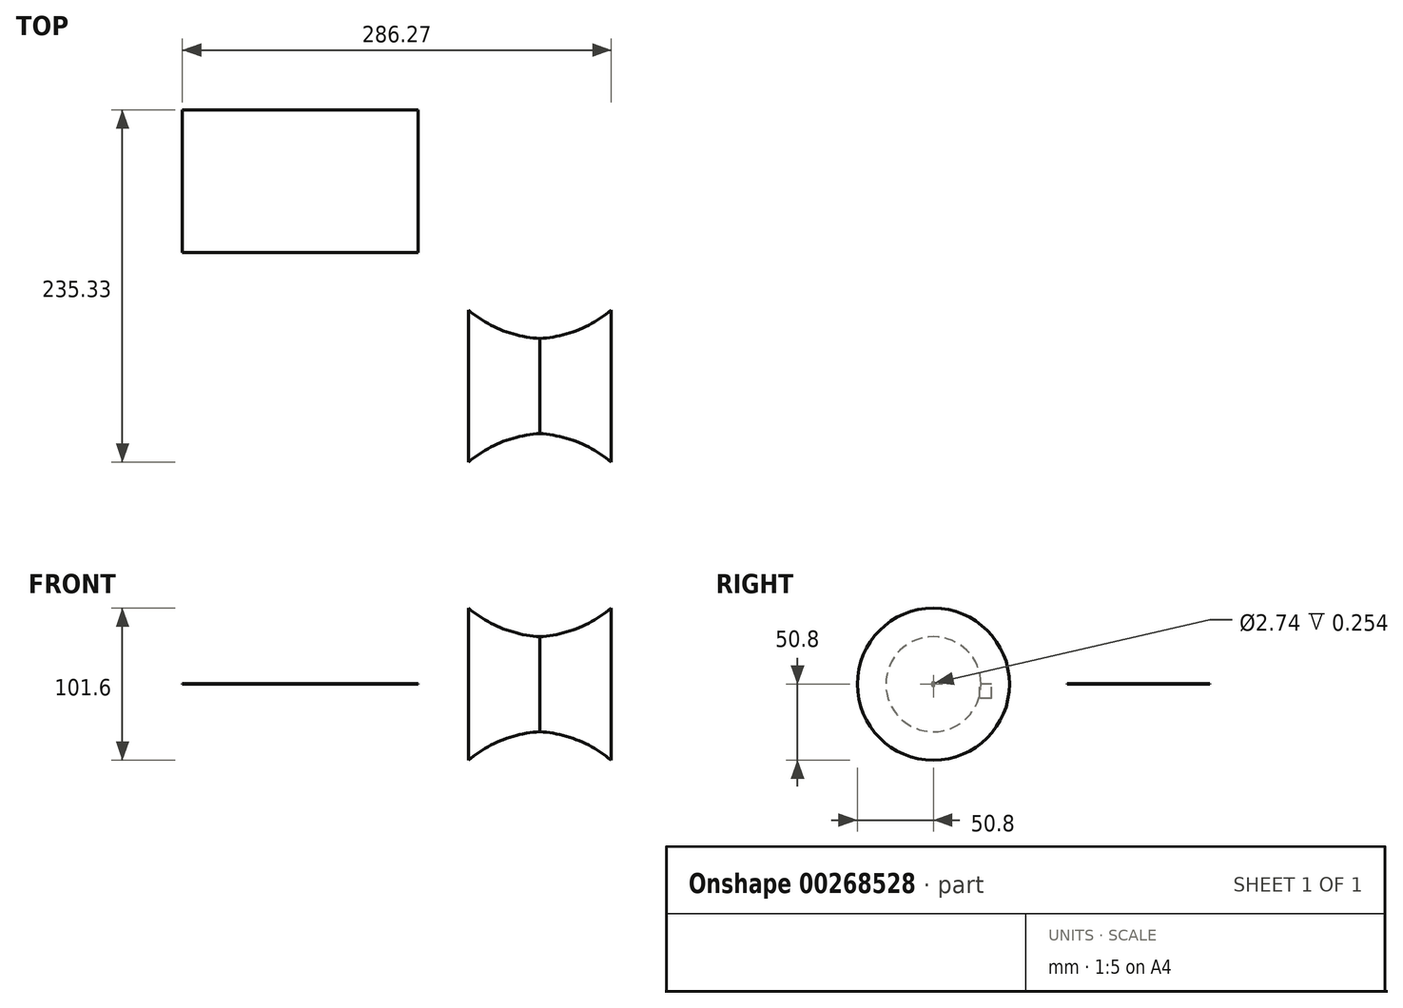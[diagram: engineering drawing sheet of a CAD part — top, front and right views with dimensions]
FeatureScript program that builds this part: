
annotation { "Feature Type Name" : "Feature", "Feature Type Description" : "" }
export const myFeature = defineFeature(function(context is Context, id is Id, definition is map)
    precondition{}
    {
        {
            var Q0;
            Q0=qCreatedBy(makeId("Top.planeOp"),FACE);
            var sketch = newSketch(context, id + "F0", { "sketchPlane" : qUnion([Q0])});
            skLineSegment(sketch, "E0", {"start": v(0, 0) * mm, "end": v(0, 50.8) * mm});
            skLineSegment(sketch, "E1", {"start": v(0, 0) * mm, "end": v(-47.63, 0) * mm});
            skLineSegment(sketch, "E2", {"start": v(-47.63, 0) * mm, "end": v(-47.63, 31.75) * mm});
            skArc(sketch, "E3", {"start": v(-47.63, 31.75) * mm, "mid": v(-22.26, 37.4) * mm, "end": v(0, 50.8) * mm});
            skSolve(sketch);
        }
        {
            var Q0;
            Q0 = qSketchRegion(id + "F0", true);
            var Q1;
            Q1=sQuery(id+"F0.wireOp",EDGE,"E1");
            revolve(context, id + "F1", {"entities" : qUnion([Q0]), "axis" : qUnion([Q1]), "revolveType" : RevolveType.FULL});
        }
        {
            var Q0;
            Q0=makeQuery(id+"F1.opRevolve","SWEPT_BODY",BODY,{"disambiguationData":[OSD([sQuery(id+"F0.wireOp",EDGE,"E0"),sQuery(id+"F0.wireOp",EDGE,"E1"),sQuery(id+"F0.wireOp",EDGE,"E2"),sQuery(id+"F0.wireOp",EDGE,"E3")])]});
            var Q1;
            Q1=makeQuery(id+"F1.opRevolve","SWEPT_FACE",FACE,{"disambiguationData":[OSD([sQuery(id+"F0.wireOp",EDGE,"E2")])]});
            mirror(context, id + "F2", {"operationType" : NewBodyOperationType.ADD, "entities" : qUnion([Q0]), "mirrorPlane" : qUnion([Q1])});
        }
        {
            var Q0;
            Q0=makeQuery(id+"F2.opPattern","COPY",FACE,{"derivedFrom":makeQuery(id+"F1.opRevolve","SWEPT_FACE",FACE,{"disambiguationData":[OSD([sQuery(id+"F0.wireOp",EDGE,"E0")])]}),"instanceName":"1"});
            var sketch = newSketch(context, id + "F3", { "sketchPlane" : qUnion([Q0])});
            skLineSegment(sketch, "E4.bottom", {"start": v(-38.84, -9.39) * mm, "end": v(-31, -9.39) * mm});
            skLineSegment(sketch, "E4.top", {"start": v(-38.84, 0) * mm, "end": v(-31, 0) * mm});
            skLineSegment(sketch, "E4.left", {"start": v(-38.84, -9.39) * mm, "end": v(-38.84, 0) * mm});
            skLineSegment(sketch, "E4.right", {"start": v(-31, -9.39) * mm, "end": v(-31, 0) * mm});
            skSolve(sketch);
        }
        {
            var Q0;
            Q0 = qSketchRegion(id + "F3", true);
            extrude(context, id + "F4", {"entities" : qUnion([Q0]), "operationType" : NewBodyOperationType.REMOVE, "oppositeDirection" : true, "depth" : 0.25 * mm});
        }
        {
            var Q0;
            Q0=makeQuery(id+"F2.opPattern","COPY",FACE,{"derivedFrom":makeQuery(id+"F1.opRevolve","SWEPT_FACE",FACE,{"disambiguationData":[OSD([sQuery(id+"F0.wireOp",EDGE,"E0")])]}),"instanceName":"1"});
            var sketch = newSketch(context, id + "F5", { "sketchPlane" : qUnion([Q0])});
            skCircle(sketch, "E5", {"center": v(0, 0) * mm, "radius": 1.37 * mm});
            skSolve(sketch);
        }
        {
            var Q0;
            Q0 = qSketchRegion(id + "F5", true);
            extrude(context, id + "F6", {"entities" : qUnion([Q0]), "operationType" : NewBodyOperationType.REMOVE, "oppositeDirection" : true, "depth" : 0.25 * mm});
        }
        {
            var Q0;
            Q0=qCreatedBy(makeId("Top.planeOp"),FACE);
            var sketch = newSketch(context, id + "F7", { "sketchPlane" : qUnion([Q0])});
            skLineSegment(sketch, "E6.bottom", {"start": v(-286.27, 184.53) * mm, "end": v(-128.79, 184.53) * mm});
            skLineSegment(sketch, "E6.top", {"start": v(-286.27, 89.28) * mm, "end": v(-128.79, 89.28) * mm});
            skLineSegment(sketch, "E6.left", {"start": v(-286.27, 184.53) * mm, "end": v(-286.27, 89.28) * mm});
            skLineSegment(sketch, "E6.right", {"start": v(-128.79, 184.53) * mm, "end": v(-128.79, 89.28) * mm});
            skSolve(sketch);
        }
        {
            var Q0;
            Q0 = qSketchRegion(id + "F7", true);
            extrude(context, id + "F8", {"entities" : qUnion([Q0]), "depth" : 0.25 * mm});
        }
    });
